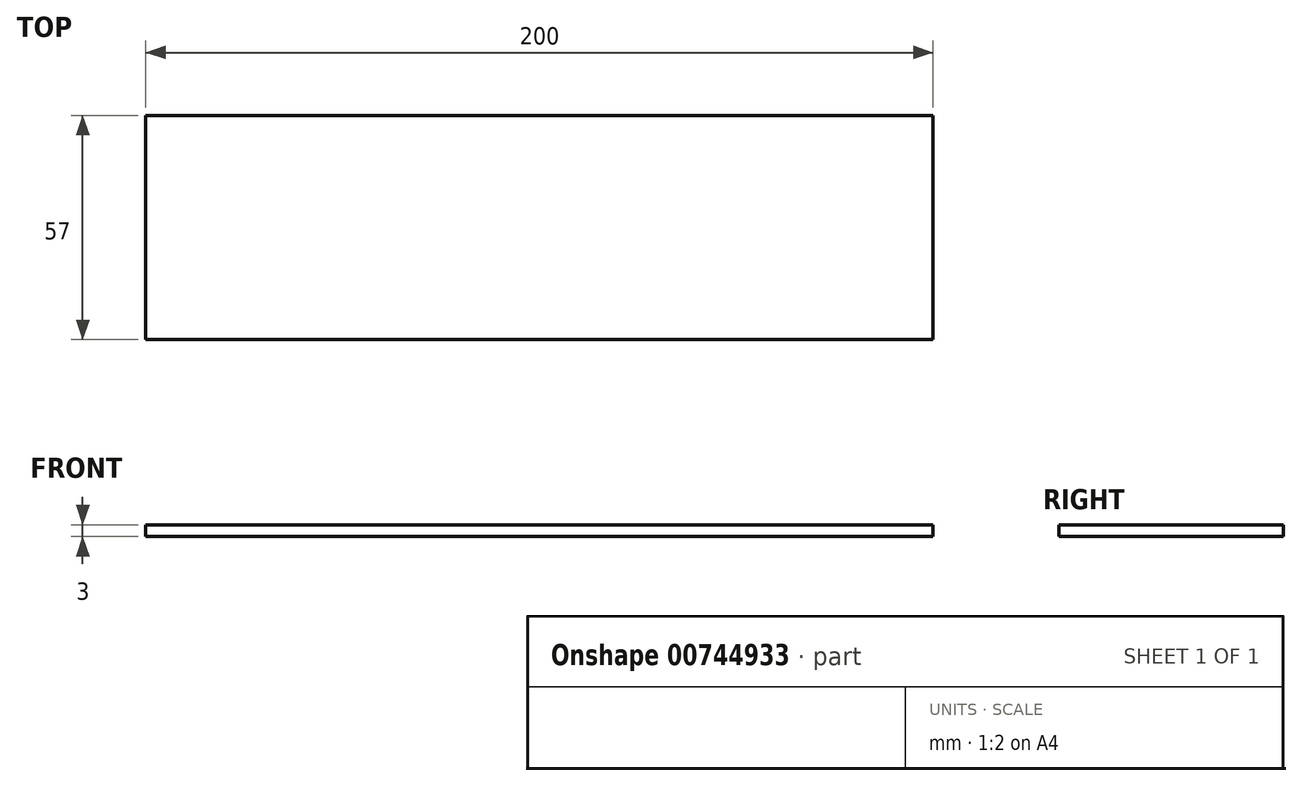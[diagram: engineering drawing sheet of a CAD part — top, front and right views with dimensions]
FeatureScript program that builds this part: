
annotation { "Feature Type Name" : "Feature", "Feature Type Description" : "" }
export const myFeature = defineFeature(function(context is Context, id is Id, definition is map)
    precondition{}
    {
        {
            var Q0;
            Q0=qCreatedBy(makeId("Top.planeOp"),FACE);
            var sketch = newSketch(context, id + "F0", { "sketchPlane" : qUnion([Q0])});
            skLineSegment(sketch, "E0", {"start": v(0, 0) * mm, "end": v(200, 0) * mm});
            skLineSegment(sketch, "E1", {"start": v(200, 0) * mm, "end": v(200, -57) * mm});
            skLineSegment(sketch, "E2", {"start": v(200, -57) * mm, "end": v(0, -57) * mm});
            skLineSegment(sketch, "E3", {"start": v(0, -57) * mm, "end": v(0, 0) * mm});
            skLineSegment(sketch, "E4", {"start": v(74.6, 5) * mm, "end": v(114.6, 5) * mm});
            skLineSegment(sketch, "E5", {"start": v(114.6, 5) * mm, "end": v(114.6, 0) * mm});
            skLineSegment(sketch, "E6", {"start": v(114.6, 0) * mm, "end": v(74.6, 0) * mm});
            skLineSegment(sketch, "E7", {"start": v(74.6, 0) * mm, "end": v(74.6, 5) * mm});
            skSolve(sketch);
        }
        {
            var Q0;
            {var subQ0=sQuery(id+"F0.wireOp",EDGE,"E1");Q0=makeQuery(id+"F0.imprint","IMPRINT",FACE,{"disambiguationData":[TD([[makeQuery(id+"F0.imprint","IMPRINT",EDGE,{"derivedFrom":subQ0}),-1.0]])]});}
            extrude(context, id + "F1", {"entities" : qUnion([Q0]), "depth" : 3 * mm, "offsetDistance" : 25 * mm});
        }
        {
            var Q0;
            Q0=sQuery(id+"F0.wireOp",EDGE,"E7");
            var Q1;
            Q1=sQuery(id+"F0.wireOp",EDGE,"E6");
            var Q2;
            Q2=sQuery(id+"F0.wireOp",EDGE,"E4");
            var Q3;
            Q3=sQuery(id+"F0.wireOp",EDGE,"E5");
            extrude(context, id + "F2", {"bodyType" : ToolBodyType.SURFACE, "surfaceEntities" : qUnion([Q0, Q1, Q2, Q3]), "depth" : 3 * mm, "offsetDistance" : 25 * mm});
        }
    });
